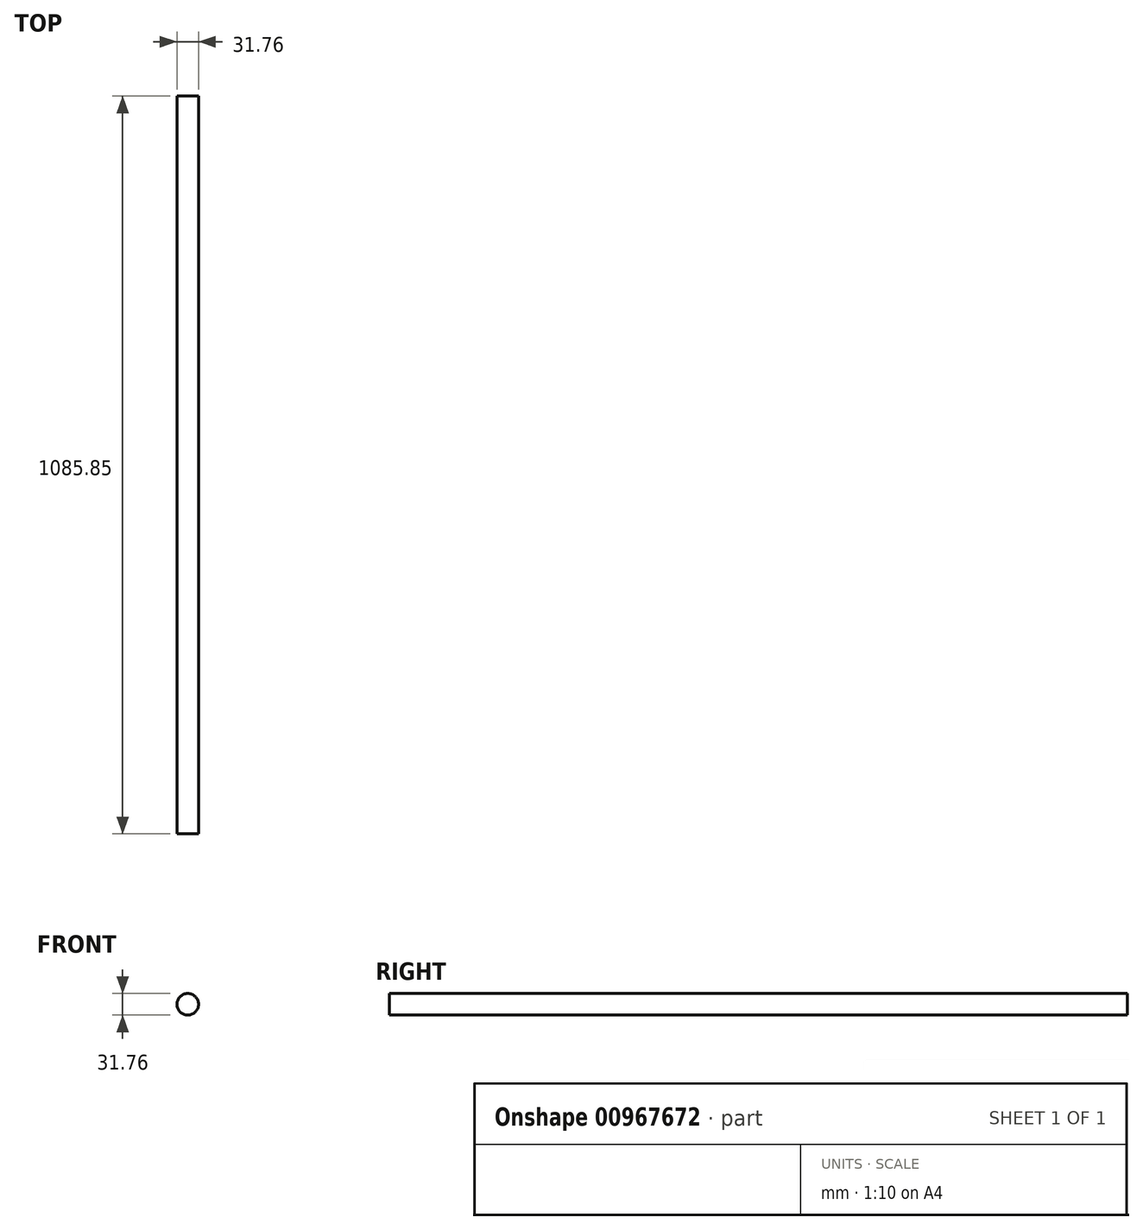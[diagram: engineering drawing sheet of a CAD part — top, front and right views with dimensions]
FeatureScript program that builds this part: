
annotation { "Feature Type Name" : "Feature", "Feature Type Description" : "" }
export const myFeature = defineFeature(function(context is Context, id is Id, definition is map)
    precondition{}
    {
        {
            var Q0;
            Q0=qCreatedBy(makeId("Front.planeOp"),FACE);
            var sketch = newSketch(context, id + "F0", { "sketchPlane" : qUnion([Q0])});
            skCircle(sketch, "E0", {"center": v(0, 0) * mm, "radius": 15.88 * mm});
            skSolve(sketch);
        }
        {
            var Q0;
            Q0 = qSketchRegion(id + "F0", true);
            extrude(context, id + "F1", {"entities" : qUnion([Q0]), "depth" : 1085.85 * mm, "offsetDistance" : 25.4 * mm});
        }
    });
